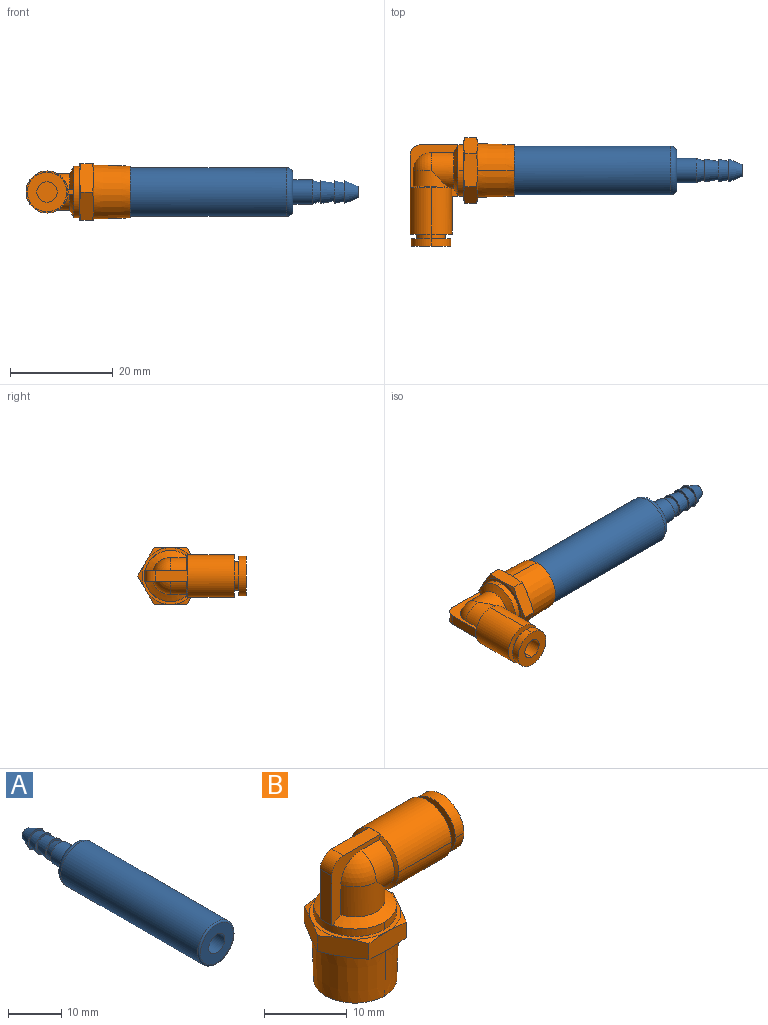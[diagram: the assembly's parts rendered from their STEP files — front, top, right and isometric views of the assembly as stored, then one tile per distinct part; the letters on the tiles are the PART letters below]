
ASSEMBLY  parts=2 mates=1
PART A: 17 faces, bbox 10.3x50.8x10.3 mm
  f0: cone r=0mm half-angle=59deg, axis (0,-1,0), area 14.9mm2, adj f14,f16
  f1: cylinder r=4.76mm len=36.45mm, axis (0,1,0), area 1090.7mm2, adj f13,f15
  f2: plane 8.77x8.77mm, normal (0,-1,0), area 45.8mm2, adj f14,f15
  f3: plane 6.99x6.99mm, normal (0,1,0), area 20.8mm2, adj f11,f13
  f4: cone r=2.24mm half-angle=22.7deg, axis (0,-1,0), area 30.1mm2, adj f5,f12
  f5: plane 4.47x4.47mm, normal (0,-1,0), area 5.8mm2, adj f4,f6
  f6: cone r=2.24mm half-angle=12.7deg, axis (0,-1,0), area 26.2mm2, adj f5,f7
  f7: plane 4.47x4.47mm, normal (0,-1,0), area 5.8mm2, adj f6,f8
  f8: cone r=2.24mm half-angle=10deg, axis (0,-1,0), area 33.2mm2, adj f7,f9
  f9: plane 4.47x4.47mm, normal (0,-1,0), area 5.8mm2, adj f8,f10
  f10: cone r=2.36mm half-angle=19.5deg, axis (0,-1,0), area 22.8mm2, adj f9,f11
  f11: cylinder r=2.36mm len=4.72mm, axis (0,-1,0), area 56.5mm2, adj f3,f10
  f12: plane 2.29x2.29mm, normal (0,1,0), area 2.3mm2, adj f4,f16
  f13: torus R=3.49mm, axis (0,1,0), area 53.9mm2, adj f1,f3
  f14: cylinder r=2.15mm len=6.35mm, axis (0,-1,0), area 85.9mm2, adj f0,f2
  f15: bspline ~9.77x9.77mm, area 18mm2, adj f1,f2
  f16: cylinder r=0.76mm len=43.61mm, axis (0,1,0), area 208.8mm2, adj f0,f12
PART B: 61 faces, bbox 21.7x13.3x20.8 mm
  f0: cone r=3.6mm half-angle=60deg, axis (1,0,0), area 5.5mm2, adj f1,f2,f13,f15,f60
  f1: cylinder r=4.1mm len=9mm, axis (-1,0,0), area 115.9mm2, adj f0,f2,f3,f16,f18,f21
  f2: cylinder r=4.1mm len=9mm, axis (-1,0,0), area 114.2mm2, adj f0,f1,f3,f13,f20,f21,f24,f26
  f3: plane 8.2x8.2mm, normal (1,0,0), area 28.6mm2, adj f1,f2,f4,f5
  f4: cylinder r=2.77mm len=5.55mm, axis (-1,0,0), area 7.8mm2, adj f3,f5,f6
  f5: cylinder r=2.77mm len=5.55mm, axis (-1,0,0), area 7.8mm2, adj f3,f4,f6
  f6: plane 7.7x7.7mm, normal (-1,0,0), area 22.4mm2, adj f4,f5,f7,f8
  f7: cylinder r=3.85mm len=7.7mm, axis (-1,0,0), area 18.1mm2, adj f6,f8,f9
  f8: cylinder r=3.85mm len=7.7mm, axis (-1,0,0), area 18.1mm2, adj f6,f7,f9
  f9: plane 7.7x7.7mm, normal (1,0,0), area 34.2mm2, adj f7,f8,f10,f11
  f10: cylinder r=1.98mm len=13.3mm, axis (-1,0,0), area 82.9mm2, adj f9,f11,f12
  f11: cylinder r=1.98mm len=13.3mm, axis (-1,0,0), area 82.9mm2, adj f9,f10,f12
  f12: plane 3.97x3.97mm, normal (1,0,0), area 12.4mm2, adj f10,f11
  f13: cylinder r=3.6mm len=7.02mm, axis (0,0,1), area 31.8mm2, adj f0,f2,f14,f15,f27,f28,f60
  f14: sphere r=3.6mm, area 14.7mm2, adj f13,f15,f60
  f15: plane 9.41x8.46mm, normal (0,1,0), area 19.9mm2, adj f0,f13,f14,f16,f17,f28,f56,f57
  f16: plane 1x0.12mm, normal (1,0,0), area 0mm2, adj f1,f15,f17
  f17: plane 6.4x2mm, normal (0,0,1), area 12.8mm2, adj f15,f16,f18,f19,f58
  f18: plane 1x0.12mm, normal (1,0,0), area 0mm2, adj f1,f17,f19
  f19: plane 9.41x8.46mm, normal (0,-1,0), area 19.9mm2, adj f17,f18,f20,f21,f22,f23,f31,f57
  f20: cylinder r=3.6mm len=7.02mm, axis (0,0,1), area 31.8mm2, adj f2,f19,f21,f22,f23,f24,f31
  f21: cone r=3.6mm half-angle=60deg, axis (1,0,0), area 5.5mm2, adj f1,f2,f19,f20,f22
  f22: cylinder r=3.6mm len=6.57mm, axis (-1,0,0), area 20.3mm2, adj f19,f20,f21,f23
  f23: sphere r=3.6mm, area 14.7mm2, adj f19,f20,f22
  f24: plane 1.46x1.21mm, normal (0,-1,0), area 1.1mm2, adj f2,f20,f25,f26,f31
  f25: plane 0.5x0.03mm, normal (0,0,-1), area 0mm2, adj f24,f26,f30
  f26: plane 1.18x1mm, normal (1,0,0), area 1.2mm2, adj f2,f24,f25,f27,f32
  f27: plane 1.46x1.21mm, normal (0,1,0), area 1.1mm2, adj f2,f13,f26,f28,f32
  f28: cone r=3.6mm half-angle=60deg, axis (0,0,-1), area 19.4mm2, adj f13,f15,f27,f29,f30
  f29: cylinder r=5mm len=10mm, axis (0,0,1), area 17.3mm2, adj f28,f30,f31,f33,f56,f59
  f30: cylinder r=5mm len=10mm, axis (0,0,1), area 17.3mm2, adj f25,f28,f29,f31,f32,f33
  f31: cone r=3.6mm half-angle=60deg, axis (0,0,-1), area 19.4mm2, adj f19,f20,f24,f29,f30
  f32: plane 0.5x0.03mm, normal (0,0,-1), area 0mm2, adj f26,f27,f30
  f33: plane 11.11x11.11mm, normal (0,0,1), area 18.4mm2, adj f29,f30,f34,f36,f38,f40,f42,f44
  f34: cone r=5.55mm half-angle=75deg, axis (0,0,-1), area 2.7mm2, adj f33,f35,f45
  f35: plane 6.03x3.68mm, normal (0.87,-0.5,0), area 16.6mm2, adj f34,f36,f37,f45,f46,f51
  f36: cone r=5.55mm half-angle=75deg, axis (0,0,-1), area 2.7mm2, adj f33,f35,f37
  f37: plane 6.03x3.68mm, normal (0.87,0.5,0), area 16.6mm2, adj f35,f36,f38,f39,f51,f52
  f38: cone r=5.55mm half-angle=75deg, axis (0,0,-1), area 2.7mm2, adj f33,f37,f39
  f39: plane 6.89x3.23mm, normal (0,1,0), area 16.6mm2, adj f37,f38,f40,f41,f48,f52
  f40: cone r=5.55mm half-angle=75deg, axis (0,0,-1), area 2.7mm2, adj f33,f39,f41
  f41: plane 6.03x3.68mm, normal (-0.87,0.5,0), area 16.6mm2, adj f39,f40,f42,f43,f48,f49
  f42: cone r=5.55mm half-angle=75deg, axis (0,0,-1), area 2.7mm2, adj f33,f41,f43
  f43: plane 6.03x3.68mm, normal (-0.87,-0.5,0), area 16.6mm2, adj f41,f42,f44,f45,f49,f50
  f44: cone r=5.55mm half-angle=75deg, axis (0,0,-1), area 2.7mm2, adj f33,f43,f45
  f45: plane 6.89x3.23mm, normal (0,-1,0), area 16.6mm2, adj f34,f35,f43,f44,f46,f50
  f46: cone r=6.67mm half-angle=75deg, axis (0,0,1), area 2.7mm2, adj f35,f45,f47
  f47: plane 11.11x11.11mm, normal (0,0,-1), area 9.8mm2, adj f46,f48,f49,f50,f51,f52,f53,f54
  f48: cone r=6.67mm half-angle=75deg, axis (0,0,1), area 2.7mm2, adj f39,f41,f47
  f49: cone r=6.67mm half-angle=75deg, axis (0,0,1), area 2.7mm2, adj f41,f43,f47
  f50: cone r=6.67mm half-angle=75deg, axis (0,0,1), area 2.7mm2, adj f43,f45,f47
  f51: cone r=6.67mm half-angle=75deg, axis (0,0,1), area 2.7mm2, adj f35,f37,f47
  f52: cone r=6.67mm half-angle=75deg, axis (0,0,1), area 2.7mm2, adj f37,f39,f47
  f53: cone r=5.27mm half-angle=1.8deg, axis (0,0,1), area 115mm2, adj f47,f54,f55
  f54: cone r=5.27mm half-angle=1.8deg, axis (0,0,1), area 115mm2, adj f47,f53,f55
  f55: plane 10.09x10.09mm, normal (0,0,-1), area 79.9mm2, adj f53,f54
  f56: plane 1x0.1mm, normal (0,0,-1), area 0mm2, adj f15,f29,f57
  f57: plane 7.35x2mm, normal (-1,0,0), area 14.7mm2, adj f15,f19,f56,f58,f59
  f58: cylinder r=2mm len=2mm, axis (0,-1,0), area 6.3mm2, adj f15,f17,f19,f57
  f59: plane 1x0.1mm, normal (0,0,-1), area 0mm2, adj f19,f29,f57
  f60: cylinder r=3.6mm len=6.57mm, axis (-1,0,0), area 20.3mm2, adj f0,f13,f14,f15
PLACE A rot(axis=(-0.58,-0.58,-0.58),120deg) t=(32.19,0,0)mm
PLACE B rot(axis=(0.58,-0.58,-0.58),120deg) t=(-15.46,0,0)mm
MATE fastened B.f13 <-> A.f0  axis (1,0,0) through (-12.26,0,0)mm
